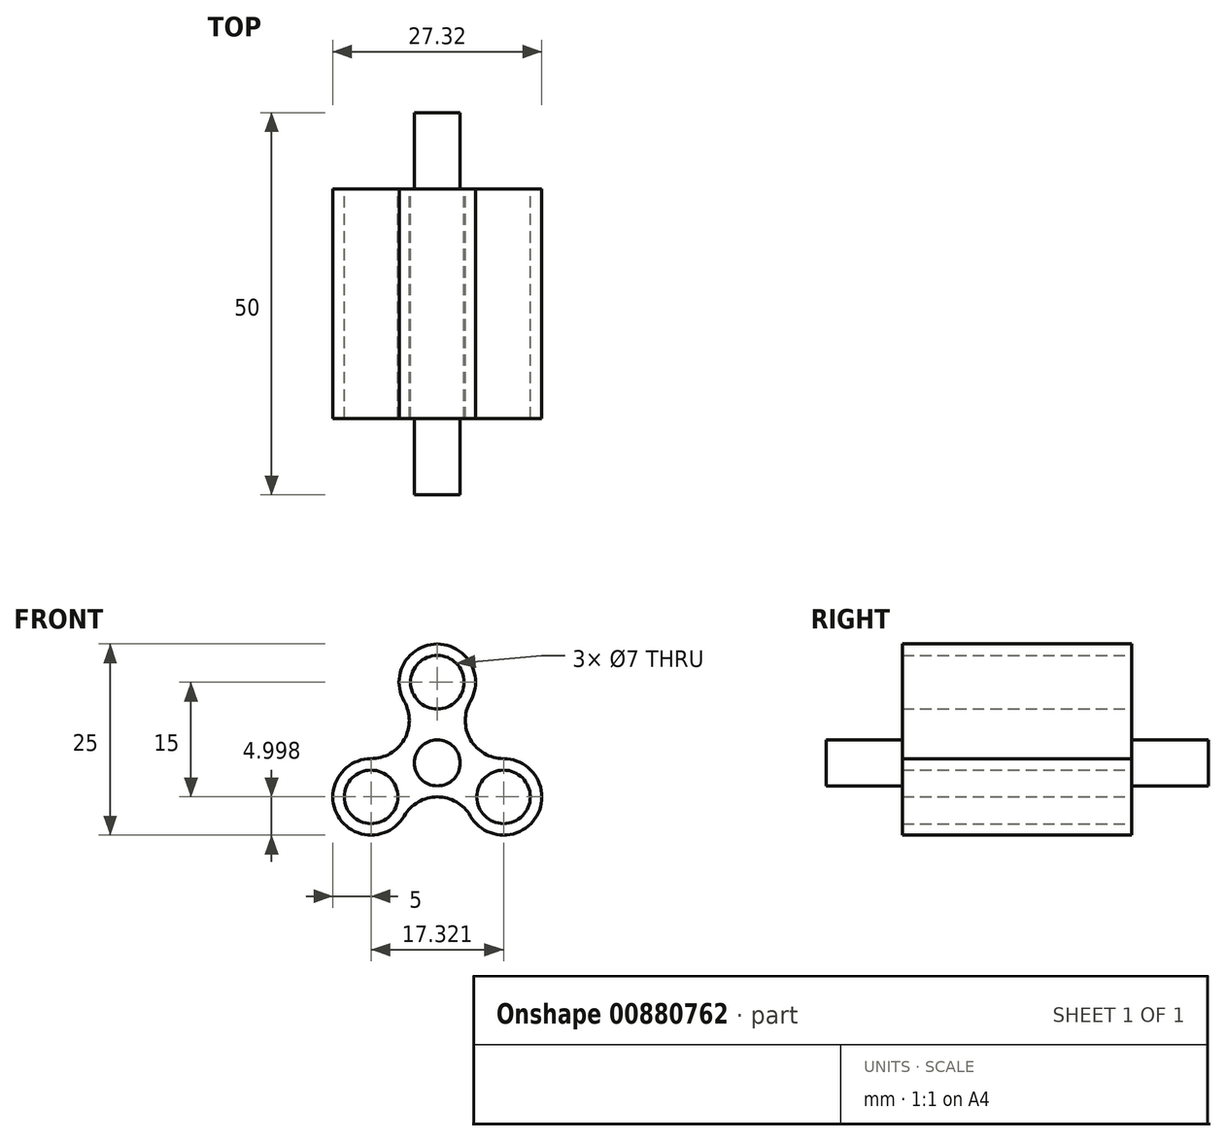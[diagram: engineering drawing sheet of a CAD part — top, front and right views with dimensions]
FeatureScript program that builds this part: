
annotation { "Feature Type Name" : "Feature", "Feature Type Description" : "" }
export const myFeature = defineFeature(function(context is Context, id is Id, definition is map)
    precondition{}
    {
        {
            var Q0;
            Q0=qCreatedBy(makeId("Front.planeOp"),FACE);
            var sketch = newSketch(context, id + "F0", { "sketchPlane" : qUnion([Q0])});
            skArc(sketch, "E0", {"start": v(4.33, 8.06) * mm, "mid": v(0, 15.56) * mm, "end": v(-4.33, 8.06) * mm});
            skArc(sketch, "E1.1.0", {"start": v(4.33, 8.06) * mm, "mid": v(4.33, 3.06) * mm, "end": v(8.66, 0.56) * mm});
            skCircle(sketch, "E1.2.0", {"center": v(8.66, -4.44) * mm, "radius": 5 * mm});
            skPoint(sketch, "E1.center", {"position": v(0, 0.56) * mm});
            skLineSegment(sketch, "E1.anchor1", {"start": v(0, 0.56) * mm, "end": v(0, 10.56) * mm, "construction": true});
            skLineSegment(sketch, "E1.anchor2", {"start": v(0, 0.56) * mm, "end": v(0, 10.56) * mm, "construction": true});
            skArc(sketch, "E2.1.3.0", {"start": v(4.33, -6.94) * mm, "mid": v(0, -4.44) * mm, "end": v(-4.33, -6.94) * mm});
            skCircle(sketch, "E3.1.4.0", {"center": v(-8.66, -4.44) * mm, "radius": 5 * mm});
            skArc(sketch, "E3.1.5.0", {"start": v(-8.66, 0.56) * mm, "mid": v(-4.33, 3.06) * mm, "end": v(-4.33, 8.06) * mm});
            skCircle(sketch, "E3.1.6.0", {"center": v(0, 10.56) * mm, "radius": 5 * mm});
            skCircle(sketch, "E4", {"center": v(0, 10.56) * mm, "radius": 3.5 * mm});
            skCircle(sketch, "E5", {"center": v(8.66, -4.44) * mm, "radius": 3.5 * mm});
            skCircle(sketch, "E6", {"center": v(-8.66, -4.44) * mm, "radius": 3.5 * mm});
            skSolve(sketch);
        }
        {
            var Q0;
            Q0=qSketchRegion(id+"F0",true);
            extrude(context, id + "F1", {"entities" : qUnion([Q0]), "depth" : 30 * mm, "offsetDistance" : 25 * mm});
        }
        {
            var Q0;
            Q0=qCreatedBy(makeId("Front.planeOp"),FACE);
            var sketch = newSketch(context, id + "F2", { "sketchPlane" : qUnion([Q0])});
            skCircle(sketch, "E7", {"center": v(0, 0) * mm, "radius": 3 * mm});
            skSolve(sketch);
        }
        {
            var Q0;
            Q0=qSketchRegion(id+"F2",true);
            extrude(context, id + "F3", {"entities" : qUnion([Q0]), "operationType" : NewBodyOperationType.ADD, "depth" : 40 * mm, "offsetDistance" : 25 * mm, "hasSecondDirection" : true, "secondDirectionOppositeDirection" : true, "secondDirectionDepth" : 10 * mm});
        }
    });
